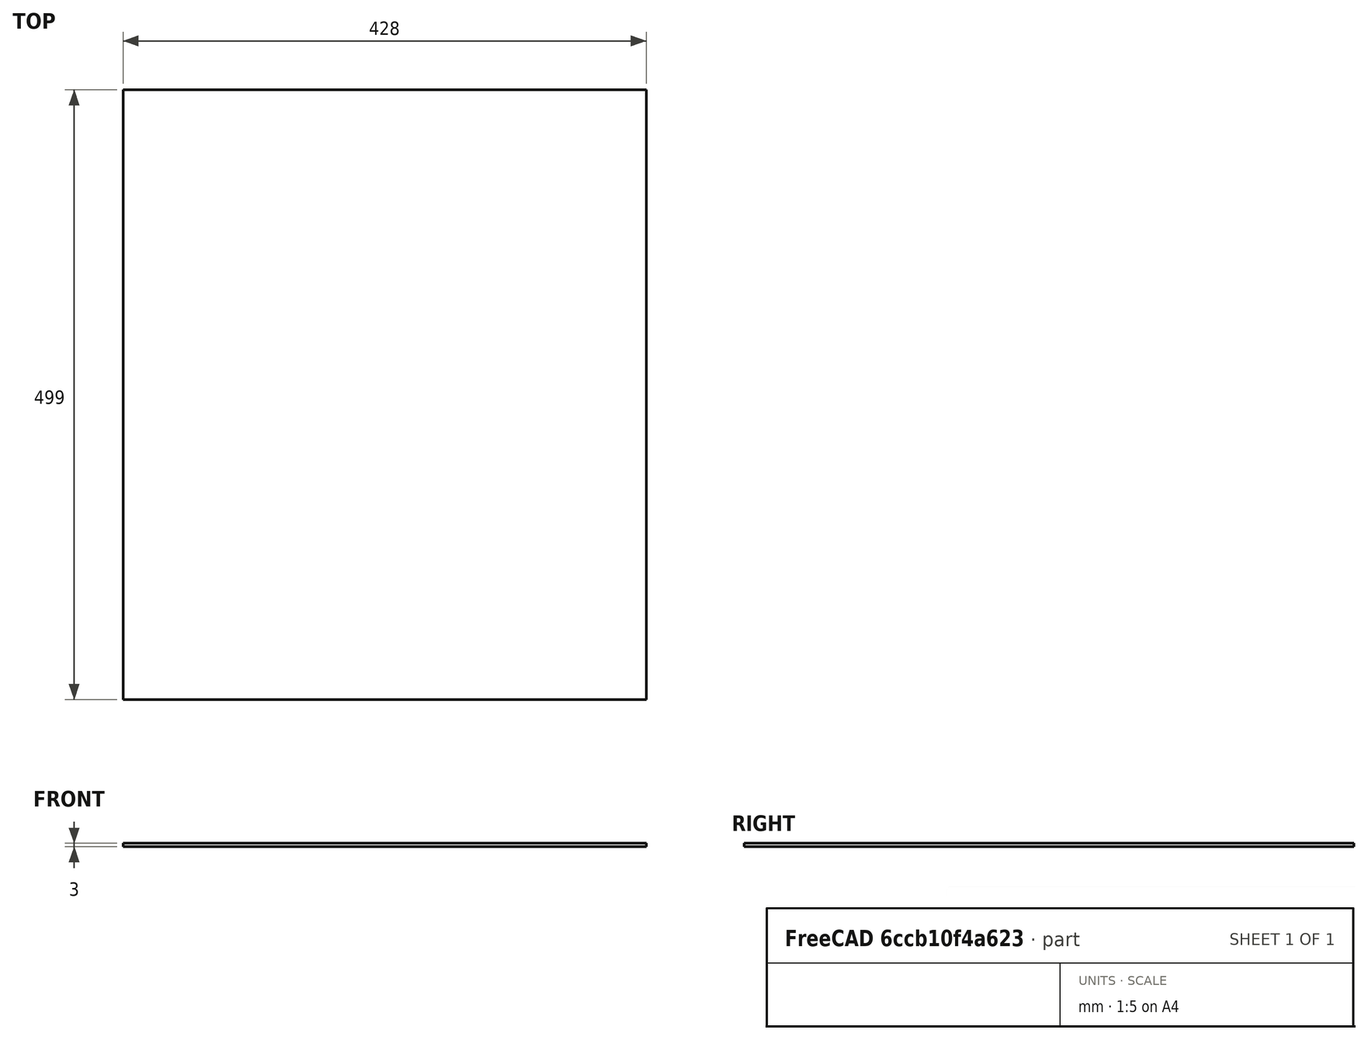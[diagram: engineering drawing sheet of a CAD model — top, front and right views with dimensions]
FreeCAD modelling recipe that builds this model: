
FCSTD DOCUMENT  (FreeCAD 0.19R)
Label: panj
License: All rights reserved
LicenseURL: http://en.wikipedia.org/wiki/All_rights_reserved
objects: App::Link×9, PartDesign::CoordinateSystem×4, App::DocumentObjectGroup×3, TechDraw::DrawSVGTemplate×3, TechDraw::DrawViewPart×3, TechDraw::DrawPage×3, App::Part×2, TechDraw::DrawViewSection×2, App::FeaturePython×1, Sketcher::SketchObject×1, PartDesign::Pad×1, PartDesign::Body×1
note: 8 computed .brp shape members not serialized (recipe doc carries the construction recipe); baked Part::Feature solids carry a one-line shape summary decoded from their .brp
EXTERNAL_REF file=podnica_ohisje.FCStd obj=LCS_bottom
EXTERNAL_REF file=podnica_ohisje.FCStd obj=Assembly
EXTERNAL_REF file=podnica_ohisje.FCStd obj=LCS_insert_low
EXTERNAL_REF file=smukalnik.FCStd obj=LCS_podnica
EXTERNAL_REF file=smukalnik.FCStd obj=Assembly
EXTERNAL_REF file=podnica_ohisje.FCStd obj=LCS_insert
EXTERNAL_REF file=smukalnik_mreza.FCStd obj=LCS_spreaj
EXTERNAL_REF file=smukalnik_mreza.FCStd obj=Assembly
EXTERNAL_REF file=podnica_ohisje.FCStd obj=LCS_pokrovcek
EXTERNAL_REF file=podnica_pokrovcek.FCStd obj=LCS_Origin
EXTERNAL_REF file=podnica_pokrovcek.FCStd obj=Assembly
EXTERNAL_REF file=naklada.FCStd obj=LCS_Origin
EXTERNAL_REF file=podnica_ohisje.FCStd obj=LCS_Origin
EXTERNAL_REF file=naklada.FCStd obj=Assembly
EXTERNAL_REF file=naklada.FCStd obj=LCS_1
EXTERNAL_REF file=naklada_nizka.FCStd obj=LCS_Origin
EXTERNAL_REF file=naklada_nizka.FCStd obj=Assembly
EXTERNAL_REF file=naklada_nizka.FCStd obj=LCS_1
EXTERNAL_REF file=pokrov.FCStd obj=LCS_botton
EXTERNAL_REF file=pokrov.FCStd obj=Assembly
EXTERNAL_REF file=pokrov.FCStd obj=LCS_1
EXTERNAL_REF file=streha.FCStd obj=LCS_Origin
EXTERNAL_REF file=streha.FCStd obj=Assembly

FEATURE [PartDesign::CoordinateSystem] LCS_Origin
  AttacherType = Attacher::AttachEngine3D
  MapMode = 2
  Support = -> [X_Axis]
FEATURE [App::FeaturePython] Variables  # WARN: FeaturePython — macro-defined, semantics opaque (R4)
  Type = App::PropertyContainer
FEATURE [App::DocumentObjectGroup] Constraints
FEATURE [App::DocumentObjectGroup] Configurations
FEATURE [App::Link] podnica_ohisje
  AttachedBy = #LCS_bottom
  AttachedTo = Parent Assembly#LCS_Origin
  LinkPlacement = pos=(0,0,120) rot=(0,0,1;0rad)
  LinkedObject = -> <external podnica_ohisje.FCStd>#Assembly
  Placement = pos=(0,0,120) rot=(0,0,1;0rad)
  SolverId = Asm4EE
  expr: Placement = LCS_Origin.Placement * AttachmentOffset * podnica_ohisje#LCS_bottom.Placement ^ -1
FEATURE [App::Link] smukalnik
  AttachedBy = #LCS_podnica
  AttachedTo = podnica_ohisje#LCS_insert_low
  LinkPlacement = pos=(0,-234,65) rot=(0,0,1;0rad)
  LinkedObject = -> <external smukalnik.FCStd>#Assembly
  Placement = pos=(0,-234,65) rot=(0,0,1;0rad)
  SolverId = Asm4EE
  expr: Placement = podnica_ohisje.Placement * podnica_ohisje#LCS_insert_low.Placement * AttachmentOffset * smukalnik#LCS_podnica.Placement ^ -1
FEATURE [App::Link] smukalnik_mreza
  AttachedBy = #LCS_spreaj
  AttachedTo = podnica_ohisje#LCS_insert
  LinkPlacement = pos=(0,18.5,35) rot=(0,0,1;0rad)
  LinkedObject = -> <external smukalnik_mreza.FCStd>#Assembly
  Placement = pos=(0,18.5,35) rot=(0,0,1;0rad)
  SolverId = Asm4EE
  expr: Placement = podnica_ohisje.Placement * podnica_ohisje#LCS_insert.Placement * AttachmentOffset * smukalnik_mreza#LCS_spreaj.Placement ^ -1
FEATURE [App::Link] podnica_pokrovcek
  AttachedBy = #LCS_Origin
  AttachedTo = podnica_ohisje#LCS_pokrovcek
  LinkPlacement = pos=(0,-252,35) rot=(0,0,1;0rad)
  LinkedObject = -> <external podnica_pokrovcek.FCStd>#Assembly
  Placement = pos=(0,-252,35) rot=(0,0,1;0rad)
  SolverId = Asm4EE
  expr: Placement = podnica_ohisje.Placement * podnica_ohisje#LCS_pokrovcek.Placement * AttachmentOffset * podnica_pokrovcek#LCS_Origin.Placement ^ -1
FEATURE [App::Link] naklada
  AttachedBy = #LCS_Origin
  AttachedTo = podnica_ohisje#LCS_Origin
  LinkPlacement = pos=(0,0,120) rot=(0,0,1;0rad)
  LinkedObject = -> <external naklada.FCStd>#Assembly
  Placement = pos=(0,0,120) rot=(0,0,1;0rad)
  SolverId = Asm4EE
  expr: Placement = podnica_ohisje.Placement * podnica_ohisje#LCS_Origin.Placement * AttachmentOffset * naklada#LCS_Origin.Placement ^ -1
FEATURE [PartDesign::CoordinateSystem] LCS_0  label="LCS_bottom"
  AttacherType = Attacher::AttachEngine3D
  MapMode = 2
  Support = -> [X_Axis001]
FEATURE [PartDesign::CoordinateSystem] LCS_0001
  AttacherType = Attacher::AttachEngine3D
  MapMode = 2
  Support = -> [X_Axis002]
FEATURE [Sketcher::SketchObject] Sketch
  FullyConstrained = true
  MapMode = 5
  Support = -> [XY_Plane002]
  sketch-geometry (4):
    g0: LineSegment StartX=-214 StartY=-249.5 StartZ=0 EndX=214 EndY=-249.5 EndZ=0
    g1: LineSegment StartX=214 StartY=-249.5 StartZ=0 EndX=214 EndY=249.5 EndZ=0
    g2: LineSegment StartX=214 StartY=249.5 StartZ=0 EndX=-214 EndY=249.5 EndZ=0
    g3: LineSegment StartX=-214 StartY=249.5 StartZ=0 EndX=-214 EndY=-249.5 EndZ=0
  constraints (10):
    c: Coincident(g0,g1)
    c: Coincident(g1,g2)
    c: Coincident(g2,g3)
    c: Coincident(g3,g0)
    c: Horizontal(g2)
    c: Vertical(g3)
    c: Symmetric(g0,g0,g-2)
    c: Symmetric(g0,g1,g-1)
    c: DistanceX(g2,g2) = 428
    c: DistanceY(g1,g1) = 499
FEATURE [PartDesign::Pad] Pad
  Direction = (1,1,1)
  Length = 3
  Length2 = 100
  Profile = -> Sketch
  Type = 0
FEATURE [PartDesign::Body] Body
  Group = -> [LCS_0001,Sketch,Pad]
  Origin = -> Origin002
  Tip = -> Pad
FEATURE [PartDesign::CoordinateSystem] LCS_1  label="LCS_up"
  AttacherType = Attacher::AttachEngine3D
  Placement = pos=(0,0,3) rot=(0,0,1;0rad)
FEATURE [App::Part] maticna_resetka
  Group = -> [LCS_0,Body,LCS_1]
  Origin = -> Origin001
FEATURE [App::DocumentObjectGroup] Parts
  Group = -> [maticna_resetka]
FEATURE [App::Link] maticna_resetka001
  AssemblyType = Part::Link
  AttachedBy = #LCS_0
  AttachedTo = naklada#LCS_1
  LinkPlacement = pos=(0,0,420) rot=(0,0,1;0rad)
  LinkedObject = -> maticna_resetka
  Placement = pos=(0,0,420) rot=(0,0,1;0rad)
  SolverId = Asm4EE
  expr: Placement = naklada.Placement * naklada#LCS_1.Placement * AttachmentOffset * LCS_0.Placement ^ -1
FEATURE [App::Link] naklada_nizka
  AttachedBy = #LCS_Origin
  AttachedTo = maticna_resetka001#LCS_1
  LinkPlacement = pos=(0,0,423) rot=(0,0,1;0rad)
  LinkedObject = -> <external naklada_nizka.FCStd>#Assembly
  Placement = pos=(0,0,423) rot=(0,0,1;0rad)
  SolverId = Asm4EE
  expr: Placement = maticna_resetka001.Placement * LCS_1.Placement * AttachmentOffset * naklada_nizka#LCS_Origin.Placement ^ -1
FEATURE [App::Link] pokrov
  AttachedBy = #LCS_botton
  AttachedTo = naklada_nizka#LCS_1
  LinkPlacement = pos=(0,0,641) rot=(0,0,1;0rad)
  LinkedObject = -> <external pokrov.FCStd>#Assembly
  Placement = pos=(0,0,641) rot=(0,0,1;0rad)
  SolverId = Asm4EE
  expr: Placement = naklada_nizka.Placement * naklada_nizka#LCS_1.Placement * AttachmentOffset * pokrov#LCS_botton.Placement ^ -1
FEATURE [App::Link] streha
  AttachedBy = #LCS_Origin
  AttachedTo = pokrov#LCS_1
  LinkPlacement = pos=(0,0,701) rot=(0,0,1;0rad)
  LinkedObject = -> <external streha.FCStd>#Assembly
  Placement = pos=(0,0,701) rot=(0,0,1;0rad)
  SolverId = Asm4EE
  expr: Placement = pokrov.Placement * pokrov#LCS_1.Placement * AttachmentOffset * streha#LCS_Origin.Placement ^ -1
FEATURE [App::Part] Assembly
  AssemblyType = Part::Link
  Group = -> [LCS_Origin,Variables,Constraints,Configurations,podnica_ohisje,smukalnik,smukalnik_mreza,podnica_pokrovcek,naklada,maticna_resetka001,naklada_nizka,pokrov,streha]
  Origin = -> Origin
  Type = Assembly
FEATURE [TechDraw::DrawSVGTemplate] Template
  EditableTexts = AVTOR=Brane Borštnik; AVTOR_2=Risal: Janez Paternoster; DATUM=6.5.2022; MERILO=1:4; NAZIV=Dadant-Blatt panj; STRAN=Stran 1/3; VIR=https://github.com/<owner>/Dadant-Blatt
  Height = 297
  Orientation = 0
  Width = 210
FEATURE [TechDraw::DrawViewPart] View
  CoarseView = false
  Direction = (0.577,-0.577,0.577)
  Focus = 100
  HardHidden = false
  IsoCount = 0
  IsoHidden = false
  IsoVisible = false
  LockPosition = false
  Perspective = false
  Rotation = 0
  Scale = 0.25
  ScaleType = 0
  SeamHidden = false
  SeamVisible = true
  SmoothHidden = false
  SmoothVisible = true
  Source = -> [Assembly]
  X = 112.091
  XDirection = (0.707,0.707,0)
  Y = 158.928
FEATURE [TechDraw::DrawPage] Page  label="Page1"
  KeepUpdated = true
  NextBalloonIndex = 1
  ProjectionType = 0
  Scale = 0.25
  Template = -> Template
  Views = -> [View]
FEATURE [TechDraw::DrawSVGTemplate] Template001
  EditableTexts = AVTOR=Brane Borštnik; AVTOR_2=Risal: Janez Paternoster; DATUM=6.5.2022; MERILO=1:3,33; NAZIV=Dadant-Blatt panj; STRAN=Stran 2/3; VIR=https://github.com/<owner>/Dadant-Blatt
  Height = 297
  Orientation = 0
  Width = 210
FEATURE [TechDraw::DrawViewPart] View002
  CoarseView = false
  Direction = (0,-1,0)
  Focus = 100
  HardHidden = false
  IsoCount = 0
  IsoHidden = false
  IsoVisible = false
  LockPosition = false
  Perspective = false
  Rotation = 0
  Scale = 0.3
  ScaleType = 0
  SeamHidden = false
  SeamVisible = true
  SmoothHidden = false
  SmoothVisible = true
  Source = -> [Assembly]
  X = -84.3792
  XDirection = (1,0,0)
  Y = 158.511
FEATURE [TechDraw::DrawViewSection] SectionView  label="Section  - "
  BaseView = -> View002
  CoarseView = false
  CutSurfaceDisplay = 2
  Direction = (-1,0,0)
  FileGeomPattern = <path>
  FileHatchPattern = <path>
  Focus = 100
  FuseBeforeCut = false
  HardHidden = false
  HatchScale = 1
  IsoCount = 0
  IsoHidden = false
  IsoVisible = false
  LockPosition = false
  NameGeomPattern = Diamant
  Perspective = false
  Rotation = 0
  Scale = 0.3
  ScaleType = 0
  SeamHidden = false
  SeamVisible = true
  SectionDirection = 0
  SectionNormal = (-1,0,0)
  SectionOrigin = (0,-25,359.5)
  SmoothHidden = false
  SmoothVisible = true
  Source = -> [Assembly]
  X = 113.76
  XDirection = (0,-1,0)
  Y = 161.014
FEATURE [TechDraw::DrawPage] Page001  label="Page2"
  KeepUpdated = true
  NextBalloonIndex = 1
  ProjectionType = 0
  Scale = 0.3
  Template = -> Template001
  Views = -> [View002,SectionView]
FEATURE [TechDraw::DrawSVGTemplate] Template002
  EditableTexts = AVTOR=Brane Borštnik; AVTOR_2=Risal: Janez Paternoster; DATUM=6.5.2022; MERILO=1:3,33; NAZIV=Dadant-Blatt panj; STRAN=Stran 3/3; VIR=https://github.com/<owner>/Dadant-Blatt
  Height = 297
  Orientation = 0
  Width = 210
FEATURE [TechDraw::DrawViewPart] View003
  CoarseView = false
  Direction = (1,0,0)
  Focus = 100
  HardHidden = false
  IsoCount = 0
  IsoHidden = false
  IsoVisible = false
  LockPosition = false
  Perspective = false
  Rotation = 0
  Scale = 0.3
  ScaleType = 0
  SeamHidden = false
  SeamVisible = true
  SmoothHidden = false
  SmoothVisible = true
  Source = -> [Assembly]
  X = -108.156
  XDirection = (0,1,0)
  Y = 148.083
FEATURE [TechDraw::DrawViewSection] SectionView001  label="Section  - 001"
  BaseView = -> View003
  CoarseView = false
  CutSurfaceDisplay = 2
  Direction = (0,-1,0)
  FileGeomPattern = <path>
  FileHatchPattern = <path>
  Focus = 100
  FuseBeforeCut = false
  HardHidden = false
  HatchScale = 1
  IsoCount = 0
  IsoHidden = false
  IsoVisible = false
  LockPosition = false
  NameGeomPattern = Diamant
  Perspective = false
  Rotation = 0
  Scale = 0.3
  ScaleType = 0
  SeamHidden = false
  SeamVisible = true
  SectionDirection = 0
  SectionNormal = (0,-1,0)
  SectionOrigin = (0,-25,359.5)
  SmoothHidden = false
  SmoothVisible = true
  Source = -> [Assembly]
  X = 111.674
  XDirection = (1,0,0)
  Y = 160.18
FEATURE [TechDraw::DrawPage] Page002  label="Page3"
  KeepUpdated = true
  NextBalloonIndex = 1
  ProjectionType = 0
  Scale = 0.3
  Template = -> Template002
  Views = -> [View003,SectionView001]
note: 4 file-system paths scrubbed to <path> (originals preserved in the JSON sidecar)

RESOLVED EXTERNAL PARTS (link-assembly join: the EXTERNAL_REF files above that resolve inside this repo's crawl, each included once):
---- part naklada.FCStd = doc fcstd_21cce96157d1 (61008 chars; too large to inline — full recipe in that document) ----
---- part naklada_nizka.FCStd = doc fcstd_ec1ecf22dc17 (61010 chars; too large to inline — full recipe in that document) ----
---- part podnica_pokrovcek.FCStd = doc fcstd_f92a410cbc04 ----
FCSTD DOCUMENT  (FreeCAD 0.19R)
Label: podnica_pokrovcek
License: All rights reserved
LicenseURL: http://en.wikipedia.org/wiki/All_rights_reserved
objects: App::Link×13, PartDesign::Line×12, TechDraw::DrawViewDimension×9, Sketcher::SketchObject×6, PartDesign::CoordinateSystem×6, TechDraw::DrawProjGroupItem×6, TechDraw::DrawRichAnno×5, App::Part×4, PartDesign::Body×3, App::DocumentObjectGroup×3, TechDraw::DrawProjGroup×3, PartDesign::Pad×2, TechDraw::DrawSVGTemplate×1, PartDesign::Pocket×1, App::FeaturePython×1, PartDesign::Revolution×1, TechDraw::DrawPage×1
note: 35 computed .brp shape members not serialized (recipe doc carries the construction recipe); baked Part::Feature solids carry a one-line shape summary decoded from their .brp

FEATURE [PartDesign::Body] Body
  Origin = -> Origin001
FEATURE [Sketcher::SketchObject] Sketch
  FullyConstrained = true
  MapMode = 5
  Placement = pos=(0,0,0) rot=(1,0,0;1.5708rad)
  Support = -> [XZ_Plane001]
  sketch-geometry (8):
    g0: LineSegment StartX=-186.5 StartY=0 StartZ=0 EndX=-186.5 EndY=68 EndZ=0
    g1: LineSegment StartX=-186.5 StartY=68 StartZ=0 EndX=186.5 EndY=68 EndZ=0
    g2: LineSegment StartX=186.5 StartY=68 StartZ=0 EndX=186.5 EndY=0 EndZ=0
    g3: LineSegment StartX=186.5 StartY=0 StartZ=0 EndX=60 EndY=0 EndZ=0
    g4: LineSegment StartX=60 StartY=0 StartZ=0 EndX=60 EndY=7 EndZ=0
    g5: LineSegment StartX=60 StartY=7 StartZ=0 EndX=-60 EndY=7 EndZ=0
    g6: LineSegment StartX=-60 StartY=7 StartZ=0 EndX=-60 EndY=0 EndZ=0
    g7: LineSegment StartX=-60 StartY=0 StartZ=0 EndX=-186.5 EndY=0 EndZ=0
  constraints (23):
    c: Vertical(g0)
    c: Coincident(g0,g1)
    c: Horizontal(g1)
    c: Coincident(g1,g2)
    c: Vertical(g2)
    c: Coincident(g2,g3)
    c: Horizontal(g3)
    c: Coincident(g3,g4)
    c: Vertical(g4)
    c: Coincident(g4,g5)
    c: Horizontal(g5)
    c: Coincident(g5,g6)
    c: Vertical(g6)
    c: Coincident(g6,g7)
    c: Coincident(g7,g0)
    c: Horizontal(g7)
    c: Symmetric(g6,g3,g-1)
    c: Horizontal(g6,g3)
    c: Equal(g7,g3)
    c: DistanceY(g4,g4) = 7  'H2'
    c: DistanceX(g5,g5) = 120  'L2'
    c: DistanceY(g0,g0) = 68  'H'
    c: DistanceX(g1,g1) = 373  'L'
FEATURE [PartDesign::Pad] Pad
  Direction = (1,1,1)
  Length = 18
  Length2 = 100
  Placement = pos=(0,0,0) rot=(1,0,0;1.5708rad)
  Profile = -> Sketch
  Reversed = true
  Type = 0
FEATURE [TechDraw::DrawSVGTemplate] Template
  EditableTexts = AVTOR=Brane Borštnik,AVTOR_2=Risal: Janez Paternoster,DATUM=6.5.2022,MATERIAL=Les, smreka,MERILO=1:2,NAZIV=Pokrovček v podnici,+3 more (map truncated)
  Height = 210
  Orientation = 1
  Width = 297
FEATURE [Sketcher::SketchObject] Sketch001
  FullyConstrained = true
  MapMode = 5
  Placement = pos=(0,0,0) rot=(1,0,0;1.5708rad)
  Support = -> [XZ_Plane001]
  sketch-geometry (23):
    g0: Circle CenterX=-165 CenterY=56 CenterZ=0 NormalX=0 NormalY=0 NormalZ=1 AngleXU=0 Radius=5.5
    g1: Circle CenterX=-135 CenterY=56 CenterZ=0 NormalX=0 NormalY=0 NormalZ=1 AngleXU=0 Radius=5.5
    g2: Circle CenterX=-105 CenterY=56 CenterZ=0 NormalX=0 NormalY=0 NormalZ=1 AngleXU=0 Radius=5.5
    g3: Circle CenterX=-75 CenterY=56 CenterZ=0 NormalX=0 NormalY=0 NormalZ=1 AngleXU=0 Radius=5.5
    g4: Circle CenterX=-45 CenterY=56 CenterZ=0 NormalX=0 NormalY=0 NormalZ=1 AngleXU=0 Radius=5.5
    g5: Circle CenterX=-15 CenterY=56 CenterZ=0 NormalX=0 NormalY=0 NormalZ=1 AngleXU=0 Radius=5.5
    g6: Circle CenterX=15 CenterY=56 CenterZ=0 NormalX=0 NormalY=0 NormalZ=1 AngleXU=0 Radius=5.5
    g7: Circle CenterX=45 CenterY=56 CenterZ=0 NormalX=0 NormalY=0 NormalZ=1 AngleXU=0 Radius=5.5
    g8: Circle CenterX=75 CenterY=56 CenterZ=0 NormalX=0 NormalY=0 NormalZ=1 AngleXU=0 Radius=5.5
    g9: Circle CenterX=105 CenterY=56 CenterZ=0 NormalX=0 NormalY=0 NormalZ=1 AngleXU=0 Radius=5.5
    g10: Circle CenterX=135 CenterY=56 CenterZ=0 NormalX=0 NormalY=0 NormalZ=1 AngleXU=0 Radius=5.5
    g11: Circle CenterX=165 CenterY=56 CenterZ=0 NormalX=0 NormalY=0 NormalZ=1 AngleXU=0 Radius=5.5
    g12: LineSegment StartX=-165 StartY=56 StartZ=0 EndX=-135 EndY=56 EndZ=0
    g13: LineSegment StartX=-135 StartY=56 StartZ=0 EndX=-105 EndY=56 EndZ=0
    g14: LineSegment StartX=-105 StartY=56 StartZ=0 EndX=-75 EndY=56 EndZ=0
    g15: LineSegment StartX=-75 StartY=56 StartZ=0 EndX=-45 EndY=56 EndZ=0
    g16: LineSegment StartX=-45 StartY=56 StartZ=0 EndX=-15 EndY=56 EndZ=0
    g17: LineSegment StartX=-15 StartY=56 StartZ=0 EndX=15 EndY=56 EndZ=0
    g18: LineSegment StartX=15 StartY=56 StartZ=0 EndX=45 EndY=56 EndZ=0
    g19: LineSegment StartX=45 StartY=56 StartZ=0 EndX=75 EndY=56 EndZ=0
    g20: LineSegment StartX=75 StartY=56 StartZ=0 EndX=105 EndY=56 EndZ=0
    g21: LineSegment StartX=105 StartY=56 StartZ=0 EndX=135 EndY=56 EndZ=0
    g22: LineSegment StartX=135 StartY=56 StartZ=0 EndX=165 EndY=56 EndZ=0
  constraints (50):
    c: Horizontal(g12)
    c: Coincident(g12,g13)
    c: Horizontal(g13)
    c: Coincident(g13,g14)
    c: Horizontal(g14)
    c: Coincident(g14,g15)
    c: Coincident(g15,g16)
    c: Horizontal(g16)
    c: Coincident(g16,g17)
    c: Coincident(g17,g18)
    c: Horizontal(g18)
    c: Coincident(g18,g19)
    c: Horizontal(g19)
    c: Coincident(g19,g20)
    c: Horizontal(g20)
    c: Coincident(g20,g21)
    c: Horizontal(g21)
    c: Coincident(g21,g22)
    c: Horizontal(g22)
    c: Horizontal(g15)
    c: Symmetric(g16,g17,g-2)
    c: Equal(g17,g16)
    c: Equal(g17,g15)
    c: Equal(g17,g14)
    c: Equal(g17,g13)
    c: Equal(g17,g12)
    c: Equal(g17, g18-g22) x5
    c: Coincident(g0,g12)
    c: Coincident(g1,g12)
    c: Coincident(g2,g13)
    c: Coincident(g3,g14)
    c: Coincident(g4,g15)
    c: Coincident(g5,g16)
    c: Coincident(g6,g17)
    c: Coincident(g18,g7)
    c: Coincident(g8,g19)
    c: Coincident(g9,g20)
    c: Coincident(g22,g11)
    c: Coincident(g10,g21)
    c: Equal(g5,g4)
    c: Equal(g5,g3)
    c: Equal(g5,g2)
    c: Equal(g5,g1)
    c: Equal(g5,g0)
    c: Equal(g5,g6)
    c: Equal(g6, g7-g11) x5
    c: Diameter(g0) = 11
    c: DistanceX(g17,g17) = 30
    c: DistanceX(g0,g11) = 330
    c: DistanceY(g-1,g0) = 56
FEATURE [PartDesign::Pocket] Pocket
  BaseFeature = -> Pad
  Length = 5
  Length2 = 100
  Placement = pos=(0,0,0) rot=(1,0,0;1.5708rad)
  Profile = -> Sketch001
  Type = 1
FEATURE [PartDesign::CoordinateSystem] LCS_Origin
  AttacherType = Attacher::AttachEngine3D
  MapMode = 2
  Support = -> [X_Axis002]
FEATURE [App::FeaturePython] Variables  # WARN: FeaturePython — macro-defined, semantics opaque (R4)
  Type = App::PropertyContainer
FEATURE [App::DocumentObjectGroup] Constraints
FEATURE [App::DocumentObjectGroup] Configurations
FEATURE [PartDesign::CoordinateSystem] LCS_0
  AttacherType = Attacher::AttachEngine3D
  MapMode = 2
  Support = -> [X_Axis003]
FEATURE [PartDesign::CoordinateSystem] LCS_0001
  AttacherType = Attacher::AttachEngine3D
  MapMode = 2
  Support = -> [X_Axis004]
FEATURE [Sketcher::SketchObject] Sketch004
  FullyConstrained = true
  MapMode = 5
  Placement = pos=(0,0,0) rot=(1,0,0;1.5708rad)
  Support = -> [XZ_Plane004]
  expr: Constraints[18] = Sketch.Constraints.L
  expr: Constraints[19] = Sketch.Constraints.H
  expr: Constraints[20] = Sketch.Constraints.L2
  expr: Constraints[21] = Sketch.Constraints.H2
  sketch-geometry (8):
    g0: LineSegment StartX=-186.5 StartY=68 StartZ=0 EndX=186.5 EndY=68 EndZ=0
    g1: LineSegment StartX=186.5 StartY=68 StartZ=0 EndX=186.5 EndY=0 EndZ=0
    g2: LineSegment StartX=186.5 StartY=0 StartZ=0 EndX=60 EndY=0 EndZ=0
    g3: LineSegment StartX=60 StartY=0 StartZ=0 EndX=60 EndY=7 EndZ=0
    g4: LineSegment StartX=60 StartY=7 StartZ=0 EndX=-60 EndY=7 EndZ=0
    g5: LineSegment StartX=-60 StartY=7 StartZ=0 EndX=-60 EndY=0 EndZ=0
    g6: LineSegment StartX=-60 StartY=0 StartZ=0 EndX=-186.5 EndY=0 EndZ=0
    g7: LineSegment StartX=-186.5 StartY=0 StartZ=0 EndX=-186.5 EndY=68 EndZ=0
  constraints (23):
    c: Horizontal(g0)
    c: Coincident(g0,g1)
    c: Vertical(g1)
    c: Coincident(g1,g2)
    c: Horizontal(g2)
    c: Coincident(g2,g3)
    c: Vertical(g3)
    c: Coincident(g3,g4)
    c: Horizontal(g4)
    c: Coincident(g4,g5)
    c: Vertical(g5)
    c: Coincident(g5,g6)
    c: Horizontal(g6)
    c: Coincident(g6,g7)
    c: Coincident(g7,g0)
    c: Vertical(g7)
    c: Horizontal(g5,g2)
    c: Symmetric(g2,g5,g-1)
    c: DistanceX(g0,g0) = 373
    c: DistanceY(g7,g7) = 68
    c: DistanceX(g4,g4) = 120
    c: DistanceY(g5,g5) = 7
    c: Equal(g6,g2)
FEATURE [PartDesign::Pad] Pad001
  Direction = (1,1,1)
  Length = 18
  Length2 = 100
  Placement = pos=(0,0,0) rot=(1,0,0;1.5708rad)
  Profile = -> Sketch004
  Reversed = true
  Type = 0
  expr: Length = Pad.Length
FEATURE [Sketcher::SketchObject] Sketch005
  FullyConstrained = true
  MapMode = 5
  Placement = pos=(0,0,0) rot=(0.57735,0.57735,0.57735;2.0944rad)
  Support = -> [YZ_Plane004]
  sketch-geometry (4):
    g0: LineSegment StartX=-32.6227 StartY=0 StartZ=0 EndX=17 EndY=6.1307 EndZ=0
    g1: LineSegment StartX=17 StartY=6.1307 StartZ=0 EndX=16.7548 EndY=8.11561 EndZ=0
    g2: LineSegment StartX=16.7548 StartY=8.11561 StartZ=0 EndX=-32.868 EndY=1.98491 EndZ=0
    g3: LineSegment StartX=-32.868 StartY=1.98491 StartZ=0 EndX=-32.6227 EndY=0 EndZ=0
  constraints (12):
    c: Coincident(g0,g1)
    c: Coincident(g1,g2)
    c: Coincident(g2,g3)
    c: Coincident(g3,g0)
    c: Perpendicular(g1,g0)
    c: Perpendicular(g2,g1)
    c: Perpendicular(g3,g2)
    c: Distance(g-1,g0) = 4
    c: Distance(g-1,g2) = 6
    c: DistanceX(g-1,g0) = 17
    c: Distance(g2) = 50
    c: Horizontal(g0,g-1)
FEATURE [PartDesign::Body] Body_2
  Group = -> [LCS_0001,Sketch004,Pad001,Sketch005]
  Origin = -> Origin004
  Tip = -> Pad001
FEATURE [App::Part] pokrovcek_navaden
  Group = -> [LCS_0,Body_2]
  Origin = -> Origin003
FEATURE [PartDesign::CoordinateSystem] LCS_0002
  AttacherType = Attacher::AttachEngine3D
  MapMode = 2
  Support = -> [X_Axis005]
FEATURE [PartDesign::CoordinateSystem] LCS_0003
  AttacherType = Attacher::AttachEngine3D
  MapMode = 2
  Support = -> [X_Axis006]
FEATURE [Sketcher::SketchObject] Sketch006
  FullyConstrained = true
  MapMode = 5
  Placement = pos=(0,0,0) rot=(0.57735,0.57735,0.57735;2.0944rad)
  Support = -> [YZ_Plane006]
  sketch-geometry (5):
    g0: LineSegment StartX=-32.6227 StartY=0 StartZ=0 EndX=17 EndY=6.1307 EndZ=0
    g1: LineSegment StartX=17 StartY=6.1307 StartZ=0 EndX=16.7548 EndY=8.11561 EndZ=0
    g2: LineSegment StartX=16.7548 StartY=8.11561 StartZ=0 EndX=-32.868 EndY=1.98491 EndZ=0
    g3: LineSegment StartX=-32.868 StartY=1.98491 StartZ=0 EndX=-32.6227 EndY=0 EndZ=0
    g4: LineSegment StartX=-32.6227 StartY=-4.03041 StartZ=0 EndX=17 EndY=2.10028 EndZ=0
  constraints (16):
    c: Coincident(g0,g1)
    c: Coincident(g1,g2)
    c: Coincident(g2,g3)
    c: Coincident(g3,g0)
    c: Perpendicular(g1,g0)
    c: Perpendicular(g2,g1)
    c: Perpendicular(g3,g2)
    c: Distance(g-1,g0) = 4
    c: Distance(g-1,g2) = 6
    c: DistanceX(g-1,g0) = 17
    c: Distance(g2) = 50
    c: Horizontal(g0,g-1)
    c: PointOnObject(g-1,g4)
    c: Parallel(g4,g0)
    c: Vertical(g0,g4)
    c: Vertical(g0,g4)
FEATURE [PartDesign::Revolution] Revolution
  Angle = 360
  Axis = (1.52e-14,49.6227,6.1307)
  Base = (-1e-14,-32.6227,-4.03041)
  Placement = pos=(0,0,0) rot=(0.57735,0.57735,0.57735;2.0944rad)
  Profile = -> Sketch006
  ReferenceAxis = -> Sketch006 [Axis0]
FEATURE [App::Link] pokrovcek_smukalnik  label="pokrovcek_smukalnik001"
  AssemblyType = Part::Link
  LinkedObject = -> Part
FEATURE [PartDesign::CoordinateSystem] LCS_1
  AttacherType = Attacher::AttachEngine3D
FEATURE [PartDesign::Line] HoleAxis_1
  AttacherType = Attacher::AttachEngineLine
  Length = 15.4997
  MapMode = 19
  Placement = pos=(-165,1.24e-14,56) rot=(1,0,0;1.5708rad)
  ResizeMode = 1
  Support = -> [Pocket]
FEATURE [App::Link] cevka002  label="cevka1"
  AssemblyType = Part::Link
  AttachedBy = #LCS_0002
  AttachedTo = pokrovcek_smukalnik#HoleAxis_1
  AttachmentOffset = pos=(0,0,0) rot=(1,0,0;4.71239rad)
  LinkPlacement = pos=(-165,3.73e-14,56) rot=(0,0,1;0rad)
  LinkedObject = -> cevka
  Placement = pos=(-165,3.73e-14,56) rot=(0,0,1;0rad)
  SolverId = Asm4EE
  expr: Placement = pokrovcek_smukalnik.Placement * HoleAxis_1.Placement * AttachmentOffset * LCS_0002.Placement ^ -1
FEATURE [PartDesign::Line] HoleAxis_2 .. HoleAxis_12  x11 (patterned run collapsed; names and placements below)
  AttacherType = Attacher::AttachEngineLine
  Length = 15.4997
  MapMode = 19
  ResizeMode = 1
  Support = -> [Pocket]
  placements: 11 in arithmetic series — first pos=(-135,1.24e-14,56) rot=(1,0,0;1.5708rad), step (30,0,0), last pos=(165,1.24e-14,56) rot=(1,0,0;1.5708rad)
FEATURE [App::Part] Part  label="pokrovcek_smukalnik"
  Group = -> [Body,LCS_1,Sketch001,Pocket,Pad,Sketch,HoleAxis_1,HoleAxis_2,HoleAxis_3,HoleAxis_4,HoleAxis_5,HoleAxis_6,HoleAxis_7,HoleAxis_8,HoleAxis_9,HoleAxis_10,HoleAxis_11,HoleAxis_12]
  Origin = -> Origin
FEATURE [TechDraw::DrawProjGroupItem] ProjItem  label="Front"
  CoarseView = false
  Direction = (0,-1,0)
  Focus = 100
  HardHidden = false
  IsoCount = 0
  IsoHidden = false
  IsoVisible = false
  LockPosition = true
  Perspective = false
  Rotation = 0
  RotationVector = (1,0,0)
  Scale = 0.5
  ScaleType = 2
  SeamHidden = false
  SeamVisible = true
  SmoothHidden = false
  SmoothVisible = true
  Source = -> [Part]
  Type = 0
  X = 0
  XDirection = (1,0,0)
  Y = 0
FEATURE [TechDraw::DrawProjGroupItem] ProjItem001  label="Left"
  CoarseView = false
  Direction = (-1,-1e-16,0)
  Focus = 100
  HardHidden = false
  IsoCount = 0
  IsoHidden = false
  IsoVisible = false
  LockPosition = false
  Perspective = false
  Rotation = 0
  RotationVector = (1,0,0)
  Scale = 0.5
  ScaleType = 2
  SeamHidden = false
  SeamVisible = true
  SmoothHidden = false
  SmoothVisible = true
  Source = -> [Part]
  Type = 1
  X = 127.75
  XDirection = (1e-16,-1,0)
  Y = 0
FEATURE [TechDraw::DrawProjGroup] ProjGroup
  Anchor = -> ProjItem
  AutoDistribute = true
  LockPosition = false
  ProjectionType = 0
  Rotation = 0
  Scale = 0.5
  ScaleType = 0
  Source = -> [Part]
  Views = -> [ProjItem,ProjItem001]
  X = 113.771
  Y = 141.789
  spacingX = 30
  spacingY = 15
FEATURE [TechDraw::DrawViewDimension] Dimension
  Arbitrary = false
  ArbitraryTolerances = false
  EqualTolerance = true
  FormatSpec = %.6g
  FormatSpecOverTolerance = %+.6g
  FormatSpecUnderTolerance = %+.6g
  Inverted = false
  LockPosition = false
  MeasureType = 1
  OverTolerance = 0
  References2D = -> [ProjItem001]
  Rotation = 0
  Scale = 0.5
  ScaleType = 0
  TheoreticalExact = false
  Type = 1
  UnderTolerance = 0
  X = -0.601719
  Y = 39.2636
FEATURE [TechDraw::DrawViewDimension] Dimension001
  Arbitrary = false
  ArbitraryTolerances = false
  EqualTolerance = true
  FormatSpec = %.6g
  FormatSpecOverTolerance = %+.6g
  FormatSpecUnderTolerance = %+.6g
  Inverted = false
  LockPosition = false
  MeasureType = 1
  OverTolerance = 0
  References2D = -> [ProjItem001]
  Rotation = 0
  Scale = 0.5
  ScaleType = 0
  TheoreticalExact = false
  Type = 2
  UnderTolerance = 0
  X = 16.2335
  Y = 1.80516
FEATURE [TechDraw::DrawViewDimension] Dimension002
  Arbitrary = false
  ArbitraryTolerances = false
  EqualTolerance = true
  FormatSpec = %.6g
  FormatSpecOverTolerance = %+.6g
  FormatSpecUnderTolerance = %+.6g
  Inverted = false
  LockPosition = false
  MeasureType = 1
  OverTolerance = 0
  References2D = -> [ProjItem]
  Rotation = 0
  Scale = 0.5
  ScaleType = 0
  TheoreticalExact = false
  Type = 1
  UnderTolerance = 0
  X = 0.902579
  Y = 42.5731
FEATURE [TechDraw::DrawViewDimension] Dimension003
  Arbitrary = false
  ArbitraryTolerances = false
  EqualTolerance = true
  FormatSpec = %.6g
  FormatSpecOverTolerance = %+.6g
  FormatSpecUnderTolerance = %+.6g
  Inverted = false
  LockPosition = false
  MeasureType = 1
  OverTolerance = 0
  References2D = -> [ProjItem]
  Rotation = 0
  Scale = 0.5
  ScaleType = 0
  TheoreticalExact = false
  Type = 1
  UnderTolerance = 0
  X = -2.10602
  Y = -25.8352
FEATURE [TechDraw::DrawViewDimension] Dimension004
  Arbitrary = false
  ArbitraryTolerances = false
  EqualTolerance = true
  FormatSpec = %.6g
  FormatSpecOverTolerance = %+.6g
  FormatSpecUnderTolerance = %+.6g
  Inverted = false
  LockPosition = false
  MeasureType = 1
  OverTolerance = 0
  References2D = -> [ProjItem]
  Rotation = 0
  Scale = 0.5
  ScaleType = 0
  TheoreticalExact = false
  Type = 2
  UnderTolerance = 0
  X = -36.6189
  Y = -27.5852
FEATURE [TechDraw::DrawViewDimension] Dimension005
  Arbitrary = false
  ArbitraryTolerances = false
  EqualTolerance = true
  FormatSpec = %.6g
  FormatSpecOverTolerance = %+.6g
  FormatSpecUnderTolerance = %+.6g
  Inverted = false
  LockPosition = false
  MeasureType = 1
  OverTolerance = 0
  References2D = -> [ProjItem]
  Rotation = 0
  Scale = 0.5
  ScaleType = 0
  TheoreticalExact = false
  Type = 1
  UnderTolerance = 0
  X = -0.30086
  Y = 34.1662
FEATURE [TechDraw::DrawViewDimension] Dimension006
  Arbitrary = false
  ArbitraryTolerances = false
  EqualTolerance = true
  FormatSpec = ⌀%.6g, 12x
  FormatSpecOverTolerance = %+.6g
  FormatSpecUnderTolerance = %+.6g
  Inverted = false
  LockPosition = false
  MeasureType = 1
  OverTolerance = 0
  References2D = -> [ProjItem]
  Rotation = 0
  Scale = 0.5
  ScaleType = 0
  TheoreticalExact = false
  Type = 5
  UnderTolerance = 0
  X = -75.5158
  Y = 28.5817
FEATURE [App::Link] cevka003
  AssemblyType = Part::Link
  AttachedBy = #LCS_0002
  AttachedTo = pokrovcek_smukalnik#HoleAxis_2
  AttachmentOffset = pos=(0,0,0) rot=(1,0,0;4.71239rad)
  LinkPlacement = pos=(-135,3.73e-14,56) rot=(0,0,1;0rad)
  LinkedObject = -> cevka
  Placement = pos=(-135,3.73e-14,56) rot=(0,0,1;0rad)
  SolverId = Asm4EE
  expr: Placement = pokrovcek_smukalnik.Placement * HoleAxis_2.Placement * AttachmentOffset * LCS_0002.Placement ^ -1
FEATURE [App::Link] cevka_2
  AssemblyType = Part::Link
  AttachedBy = #LCS_0002
  AttachedTo = pokrovcek_smukalnik#HoleAxis_3
  AttachmentOffset = pos=(0,0,0) rot=(1,0,0;4.71239rad)
  LinkPlacement = pos=(-105,3.73e-14,56) rot=(0,0,1;0rad)
  LinkedObject = -> cevka
  Placement = pos=(-105,3.73e-14,56) rot=(0,0,1;0rad)
  SolverId = Asm4EE
  expr: Placement = pokrovcek_smukalnik.Placement * HoleAxis_3.Placement * AttachmentOffset * LCS_0002.Placement ^ -1
FEATURE [App::Link] cevka_3
  AssemblyType = Part::Link
  AttachedBy = #LCS_0002
  AttachedTo = pokrovcek_smukalnik#HoleAxis_4
  AttachmentOffset = pos=(0,0,0) rot=(1,0,0;4.71239rad)
  LinkPlacement = pos=(-75,3.73e-14,56) rot=(0,0,1;0rad)
  LinkedObject = -> cevka
  Placement = pos=(-75,3.73e-14,56) rot=(0,0,1;0rad)
  SolverId = Asm4EE
  expr: Placement = pokrovcek_smukalnik.Placement * HoleAxis_4.Placement * AttachmentOffset * LCS_0002.Placement ^ -1
FEATURE [App::Link] cevka_4
  AssemblyType = Part::Link
  AttachedBy = #LCS_0002
  AttachedTo = pokrovcek_smukalnik#HoleAxis_5
  AttachmentOffset = pos=(0,0,0) rot=(1,0,0;4.71239rad)
  LinkPlacement = pos=(-45,3.73e-14,56) rot=(0,0,1;0rad)
  LinkedObject = -> cevka
  Placement = pos=(-45,3.73e-14,56) rot=(0,0,1;0rad)
  SolverId = Asm4EE
  expr: Placement = pokrovcek_smukalnik.Placement * HoleAxis_5.Placement * AttachmentOffset * LCS_0002.Placement ^ -1
FEATURE [App::Link] cevka_5
  AssemblyType = Part::Link
  AttachedBy = #LCS_0002
  AttachedTo = pokrovcek_smukalnik#HoleAxis_6
  AttachmentOffset = pos=(0,0,0) rot=(1,0,0;4.71239rad)
  LinkPlacement = pos=(-15,3.73e-14,56) rot=(0,0,1;0rad)
  LinkedObject = -> cevka
  Placement = pos=(-15,3.73e-14,56) rot=(0,0,1;0rad)
  SolverId = Asm4EE
  expr: Placement = pokrovcek_smukalnik.Placement * HoleAxis_6.Placement * AttachmentOffset * LCS_0002.Placement ^ -1
FEATURE [App::Link] cevka_6
  AssemblyType = Part::Link
  AttachedBy = #LCS_0002
  AttachedTo = pokrovcek_smukalnik#HoleAxis_7
  AttachmentOffset = pos=(0,0,0) rot=(1,0,0;4.71239rad)
  LinkPlacement = pos=(15,3.73e-14,56) rot=(0,0,1;0rad)
  LinkedObject = -> cevka
  Placement = pos=(15,3.73e-14,56) rot=(0,0,1;0rad)
  SolverId = Asm4EE
  expr: Placement = pokrovcek_smukalnik.Placement * HoleAxis_7.Placement * AttachmentOffset * LCS_0002.Placement ^ -1
FEATURE [App::Link] cevka_7
  AssemblyType = Part::Link
  AttachedBy = #LCS_0002
  AttachedTo = pokrovcek_smukalnik#HoleAxis_8
  AttachmentOffset = pos=(0,0,0) rot=(1,0,0;4.71239rad)
  LinkPlacement = pos=(45,3.73e-14,56) rot=(0,0,1;0rad)
  LinkedObject = -> cevka
  Placement = pos=(45,3.73e-14,56) rot=(0,0,1;0rad)
  SolverId = Asm4EE
  expr: Placement = pokrovcek_smukalnik.Placement * HoleAxis_8.Placement * AttachmentOffset * LCS_0002.Placement ^ -1
FEATURE [App::Link] cevka_8
  AssemblyType = Part::Link
  AttachedBy = #LCS_0002
  AttachedTo = pokrovcek_smukalnik#HoleAxis_9
  AttachmentOffset = pos=(0,0,0) rot=(1,0,0;4.71239rad)
  LinkPlacement = pos=(75,3.73e-14,56) rot=(0,0,1;0rad)
  LinkedObject = -> cevka
  Placement = pos=(75,3.73e-14,56) rot=(0,0,1;0rad)
  SolverId = Asm4EE
  expr: Placement = pokrovcek_smukalnik.Placement * HoleAxis_9.Placement * AttachmentOffset * LCS_0002.Placement ^ -1
FEATURE [App::Link] cevka_9
  AssemblyType = Part::Link
  AttachedBy = #LCS_0002
  AttachedTo = pokrovcek_smukalnik#HoleAxis_10
  AttachmentOffset = pos=(0,0,0) rot=(1,0,0;4.71239rad)
  LinkPlacement = pos=(105,3.73e-14,56) rot=(0,0,1;0rad)
  LinkedObject = -> cevka
  Placement = pos=(105,3.73e-14,56) rot=(0,0,1;0rad)
  SolverId = Asm4EE
  expr: Placement = pokrovcek_smukalnik.Placement * HoleAxis_10.Placement * AttachmentOffset * LCS_0002.Placement ^ -1
FEATURE [App::Link] cevka_10
  AssemblyType = Part::Link
  AttachedBy = #LCS_0002
  AttachedTo = pokrovcek_smukalnik#HoleAxis_11
  AttachmentOffset = pos=(0,0,0) rot=(1,0,0;4.71239rad)
  LinkPlacement = pos=(135,3.73e-14,56) rot=(0,0,1;0rad)
  LinkedObject = -> cevka
  Placement = pos=(135,3.73e-14,56) rot=(0,0,1;0rad)
  SolverId = Asm4EE
  expr: Placement = pokrovcek_smukalnik.Placement * HoleAxis_11.Placement * AttachmentOffset * LCS_0002.Placement ^ -1
FEATURE [App::Link] cevka_11
  AssemblyType = Part::Link
  AttachedBy = #LCS_0002
  AttachedTo = pokrovcek_smukalnik#HoleAxis_12
  AttachmentOffset = pos=(0,0,0) rot=(1,0,0;4.71239rad)
  LinkPlacement = pos=(165,3.73e-14,56) rot=(0,0,1;0rad)
  LinkedObject = -> cevka
  Placement = pos=(165,3.73e-14,56) rot=(0,0,1;0rad)
  SolverId = Asm4EE
  expr: Placement = pokrovcek_smukalnik.Placement * HoleAxis_12.Placement * AttachmentOffset * LCS_0002.Placement ^ -1
FEATURE [App::Part] Assembly
  AssemblyType = Part::Link
  Group = -> [LCS_Origin,Variables,Constraints,Configurations,pokrovcek_smukalnik,cevka002,cevka003,cevka_2,cevka_3,cevka_4,cevka_5,cevka_6,cevka_7,cevka_8,cevka_9,cevka_10,cevka_11]
  Origin = -> Origin002
  Type = Assembly
FEATURE [TechDraw::DrawProjGroupItem] ProjItem002  label="Front001"
  CoarseView = false
  Direction = (0,-1,0)
  Focus = 100
  HardHidden = false
  IsoCount = 0
  IsoHidden = false
  IsoVisible = false
  LockPosition = true
  Perspective = false
  Rotation = 0
  RotationVector = (1,0,0)
  ScaleType = 2
  SeamHidden = false
  SeamVisible = true
  SmoothHidden = false
  SmoothVisible = true
  Source = -> [pokrovcek_navaden]
  Type = 0
  X = 0
  XDirection = (1,0,0)
  Y = 0
FEATURE [TechDraw::DrawProjGroupItem] ProjItem003  label="Left001"
  CoarseView = false
  Direction = (-1,-1e-16,0)
  Focus = 100
  HardHidden = false
  IsoCount = 0
  IsoHidden = false
  IsoVisible = false
  LockPosition = false
  Perspective = false
  Rotation = 0
  RotationVector = (1,0,0)
  ScaleType = 2
  SeamHidden = false
  SeamVisible = true
  SmoothHidden = false
  SmoothVisible = true
  Source = -> [pokrovcek_navaden]
  Type = 1
  X = 112.75
  XDirection = (1e-16,-1,0)
  Y = 0
FEATURE [TechDraw::DrawProjGroup] ProjGroup001
  Anchor = -> ProjItem002
  AutoDistribute = true
  LockPosition = false
  ProjectionType = 0
  Rotation = 0
  Scale = 0.5
  ScaleType = 0
  Source = -> [pokrovcek_navaden]
  Views = -> [ProjItem002,ProjItem003]
  X = 114.804
  Y = 54.1547
  spacingX = 15
  spacingY = 15
FEATURE [Sketcher::SketchObject] Sketch007
  FullyConstrained = true
  MapMode = 5
  Placement = pos=(-9.1e-15,-32.1323,-3.96982) rot=(0.599592,0.599592,-0.530074;2.16676rad)
  Support = -> [Revolution]
FEATURE [PartDesign::Body] Body_3
  Group = -> [LCS_0003,Sketch006,Revolution,Sketch007]
  Origin = -> Origin006
  Tip = -> Revolution
FEATURE [App::Part] cevka
  Group = -> [LCS_0002,Body_3]
  Origin = -> Origin005
FEATURE [App::DocumentObjectGroup] Parts
  Group = -> [Part,pokrovcek_navaden,cevka]
FEATURE [TechDraw::DrawProjGroupItem] ProjItem007  label="Front004"
  CoarseView = false
  Direction = (0.997,-0.013,0.071)
  Focus = 100
  HardHidden = false
  IsoCount = 0
  IsoHidden = false
  IsoVisible = false
  LockPosition = true
  Perspective = false
  Rotation = 0
  RotationVector = (0.004,0.992,0.126)
  ScaleType = 2
  SeamHidden = false
  SeamVisible = true
  SmoothHidden = false
  SmoothVisible = true
  Source = -> [cevka]
  Type = 0
  X = 0
  XDirection = (0.004,0.992,0.126)
  Y = 0
FEATURE [TechDraw::DrawProjGroupItem] ProjItem008  label="Left002"
  CoarseView = false
  Direction = (-0.00396217,-0.992022,-0.126)
  Focus = 100
  HardHidden = false
  IsoCount = 0
  IsoHidden = false
  IsoVisible = false
  LockPosition = false
  Perspective = false
  Rotation = 0
  RotationVector = (1,0,0)
  ScaleType = 2
  SeamHidden = false
  SeamVisible = true
  SmoothHidden = false
  SmoothVisible = true
  Source = -> [cevka]
  Type = 1
  X = 30.568
  XDirection = (0.99739,-0.0130051,0.0710277)
  Y = 0
FEATURE [TechDraw::DrawProjGroup] ProjGroup004
  Anchor = -> ProjItem007
  AutoDistribute = true
  LockPosition = false
  ProjectionType = 0
  Rotation = 0
  Scale = 0.5
  ScaleType = 0
  Source = -> [cevka]
  Views = -> [ProjItem007,ProjItem008]
  X = 212.552
  Y = 95.1458
  spacingX = 15
  spacingY = 15
FEATURE [TechDraw::DrawViewDimension] Dimension009
  Arbitrary = false
  ArbitraryTolerances = false
  EqualTolerance = true
  FormatSpec = %.0f
  FormatSpecOverTolerance = %+.6g
  FormatSpecUnderTolerance = %+.6g
  Inverted = false
  LockPosition = false
  MeasureType = 1
  OverTolerance = 0
  References2D = -> [ProjItem007]
  Rotation = 0
  Scale = 0.5
  ScaleType = 0
  TheoreticalExact = false
  Type = 1
  UnderTolerance = 0
  X = 0.645995
  Y = 15.0715
FEATURE [TechDraw::DrawViewDimension] Dimension010
  Arbitrary = false
  ArbitraryTolerances = false
  EqualTolerance = true
  FormatSpec = ⌀%.0f
  FormatSpecOverTolerance = %+.6g
  FormatSpecUnderTolerance = %+.6g
  Inverted = false
  LockPosition = false
  MeasureType = 1
  OverTolerance = 0
  References2D = -> [ProjItem008]
  Rotation = 0
  Scale = 0.5
  ScaleType = 0
  TheoreticalExact = false
  Type = 5
  UnderTolerance = 0
  X = 13.033
  Y = 14.9402
FEATURE [TechDraw::DrawRichAnno] RichTextAnnotation
  AnnoParent = -> ProjItem007
  AnnoText = <!DOCTYPE HTML PUBLIC "-//W3C//DTD HTML 4.0//EN" "http://www.w3.org/TR/REC-html40/strict.dtd">\n<html><head><meta name="qrichtext" content="1" /><style type="text/css">\np, li { white-space: pre-wrap; }\n</style></head><body style=" font-family:'Ubuntu'; font-size:11pt; font-weight:400; font-style:normal;">\n<p style=" margin-top:0px; margin-bottom:0px; margin-left:0px; margin-right:0px; -qt-block-indent:0; text-indent:0px;"><span style=" font-size:10pt;">Cevke, 12 kom</span></p></body></html>
  LockPosition = false
  MaxWidth = -1
  Rotation = 0
  Scale = 0.5
  ScaleType = 0
  ShowFrame = false
  X = 19.8673
  Y = -10.8078
FEATURE [TechDraw::DrawRichAnno] RichTextAnnotation001
  AnnoParent = -> ProjItem
  AnnoText = <!DOCTYPE HTML PUBLIC "-//W3C//DTD HTML 4.0//EN" "http://www.w3.org/TR/REC-html40/strict.dtd">\n<html><head><meta name="qrichtext" content="1" /><style type="text/css">\np, li { white-space: pre-wrap; }\n</style></head><body style=" font-family:'Ubuntu'; font-size:11pt; font-weight:400; font-style:normal;">\n<p style=" margin-top:0px; margin-bottom:0px; margin-left:0px; margin-right:0px; -qt-block-indent:0; text-indent:0px;"><span style=" font-size:10pt;">Pokrovček za smukalnik.</span></p>\n<p style=" margin-top:0px; margin-bottom:0px; margin-left:0px; margin-right:0px; -qt-block-indent:0; text-indent:0px;"><span style=" font-size:10pt;">V luknje se vstavijo cevke,</span></p>\n<p style=" margin-top:0px; margin-bottom:0px; margin-left:0px; margin-right:0px; -qt-block-indent:0; text-indent:0px;"><span style=" font-size:10pt;">ki naj bodo obrnjene rahlo navzdol</span></p></body></html>
  LockPosition = false
  MaxWidth = -1
  Rotation = 0
  Scale = 0.5
  ScaleType = 0
  ShowFrame = false
  X = 49.9067
  Y = -3.81453
FEATURE [TechDraw::DrawRichAnno] RichTextAnnotation002
  AnnoParent = -> ProjItem002
  AnnoText = <!DOCTYPE HTML PUBLIC "-//W3C//DTD HTML 4.0//EN" "http://www.w3.org/TR/REC-html40/strict.dtd">\n<html><head><meta name="qrichtext" content="1" /><style type="text/css">\np, li { white-space: pre-wrap; }\n</style></head><body style=" font-family:'Ubuntu'; font-size:11pt; font-weight:400; font-style:normal;">\n<p style=" margin-top:0px; margin-bottom:0px; margin-left:0px; margin-right:0px; -qt-block-indent:0; text-indent:0px;"><span style=" font-size:10pt;">Navaden pokrovček na podnici</span></p></body></html>
  LockPosition = false
  MaxWidth = -1
  Rotation = 0
  Scale = 0.5
  ScaleType = 0
  ShowFrame = false
  X = 0
  Y = 0
FEATURE [TechDraw::DrawRichAnno] RichTextAnnotation003
  AnnoParent = -> ProjItem
  AnnoText = <!DOCTYPE HTML PUBLIC "-//W3C//DTD HTML 4.0//EN" "http://www.w3.org/TR/REC-html40/strict.dtd">\n<html><head><meta name="qrichtext" content="1" /><style type="text/css">\np, li { white-space: pre-wrap; }\n</style></head><body style=" font-family:'Ubuntu'; font-size:11pt; font-weight:400; font-style:normal;">\n<p style=" margin-top:0px; margin-bottom:0px; margin-left:0px; margin-right:0px; -qt-block-indent:0; text-indent:0px;"><span style=" font-size:10pt;">1 kom</span></p></body></html>
  LockPosition = false
  MaxWidth = -1
  Rotation = 0
  Scale = 0.5
  ScaleType = 0
  ShowFrame = false
  X = -76.7192
  Y = -6.01719
FEATURE [TechDraw::DrawRichAnno] RichTextAnnotation004
  AnnoParent = -> ProjItem002
  AnnoText = <!DOCTYPE HTML PUBLIC "-//W3C//DTD HTML 4.0//EN" "http://www.w3.org/TR/REC-html40/strict.dtd">\n<html><head><meta name="qrichtext" content="1" /><style type="text/css">\np, li { white-space: pre-wrap; }\n</style></head><body style=" font-family:'Ubuntu'; font-size:11pt; font-weight:400; font-style:normal;">\n<p style=" margin-top:0px; margin-bottom:0px; margin-left:0px; margin-right:0px; -qt-block-indent:0; text-indent:0px;"><span style=" font-size:10pt;">1 kom</span></p></body></html>
  LockPosition = false
  MaxWidth = -1
  Rotation = 0
  Scale = 0.5
  ScaleType = 0
  ShowFrame = false
  X = -78.8252
  Y = -6.01719
FEATURE [TechDraw::DrawPage] Page
  KeepUpdated = true
  NextBalloonIndex = 1
  ProjectionType = 0
  Scale = 0.5
  Template = -> Template
  Views = -> [ProjGroup,Dimension,Dimension001,Dimension002,Dimension003,Dimension004,Dimension005,Dimension006,ProjGroup001,ProjGroup004,Dimension009,Dimension010,RichTextAnnotation,RichTextAnnotation001,RichTextAnnotation002,RichTextAnnotation003,RichTextAnnotation004]
---- part streha.FCStd = doc fcstd_2c72739222b1 ----
FCSTD DOCUMENT  (FreeCAD 0.19R)
Label: streha
License: All rights reserved
LicenseURL: http://en.wikipedia.org/wiki/All_rights_reserved
objects: Sketcher::SketchObject×8, PartDesign::CoordinateSystem×7, TechDraw::DrawProjGroupItem×6, TechDraw::DrawViewDimension×6, App::Link×5, PartDesign::Pocket×4, App::Part×4, App::DocumentObjectGroup×3, PartDesign::Pad×3, PartDesign::Body×3, TechDraw::DrawProjGroup×3, TechDraw::DrawRichAnno×3, App::FeaturePython×1, TechDraw::DrawSVGTemplate×1, TechDraw::DrawViewPart×1, TechDraw::DrawPage×1
note: 32 computed .brp shape members not serialized (recipe doc carries the construction recipe); baked Part::Feature solids carry a one-line shape summary decoded from their .brp

FEATURE [PartDesign::CoordinateSystem] LCS_Origin
  AttacherType = Attacher::AttachEngine3D
  MapMode = 2
  Support = -> [X_Axis]
FEATURE [App::FeaturePython] Variables  # WARN: FeaturePython — macro-defined, semantics opaque (R4)
  Type = App::PropertyContainer
  bottom_thickness = 18
  inner_depth = 450
  inner_width = 375
  wall_thickness = 27
FEATURE [App::DocumentObjectGroup] Constraints
FEATURE [App::DocumentObjectGroup] Configurations
FEATURE [PartDesign::CoordinateSystem] LCS_0004
  AttacherType = Attacher::AttachEngine3D
  MapMode = 2
  Support = -> [X_Axis005]
FEATURE [PartDesign::CoordinateSystem] LCS_0005
  AttacherType = Attacher::AttachEngine3D
  MapMode = 2
  Support = -> [X_Axis006]
FEATURE [Sketcher::SketchObject] Sketch003  label="Sketch004"
  FullyConstrained = true
  MapMode = 5
  Placement = pos=(0,0,0) rot=(1,0,0;1.5708rad)
  Support = -> [XZ_Plane006]
  expr: Constraints[12] = Variables.inner_width / 2 + Variables.wall_thickness
  sketch-geometry (6):
    g0: LineSegment StartX=214.5 StartY=0 StartZ=0 EndX=218.5 EndY=0 EndZ=0
    g1: LineSegment StartX=218.5 StartY=0 StartZ=0 EndX=218.5 EndY=-8 EndZ=0
    g2: LineSegment StartX=218.5 StartY=-8 StartZ=0 EndX=226.5 EndY=-8 EndZ=0
    g3: LineSegment StartX=226.5 StartY=-8 StartZ=0 EndX=226.5 EndY=25.6324 EndZ=0
    g4: LineSegment StartX=214.5 StartY=30 StartZ=0 EndX=214.5 EndY=0 EndZ=0
    g5: LineSegment StartX=214.5 StartY=30 StartZ=0 EndX=226.5 EndY=25.6324 EndZ=0
  constraints (18):
    c: Horizontal(g0)
    c: Coincident(g0,g1)
    c: Vertical(g1)
    c: Coincident(g1,g2)
    c: Horizontal(g2)
    c: Coincident(g2,g3)
    c: Vertical(g3)
    c: Coincident(g4,g0)
    c: Vertical(g4)
    c: DistanceX(g0,g0) = 4  'c'
    c: DistanceY(g1,g1) = 8  'd'
    c: Horizontal(g0,g-1)
    c: DistanceX(g-1,g0) = 214.5
    c: DistanceX(g0,g2) = 12  'a'
    c: DistanceY(g4,g4) = 30  'b'
    c: Coincident(g5,g4)
    c: Coincident(g5,g3)
    c: Angle(g5) = -0.349066  'e'
FEATURE [PartDesign::Pad] Pad002
  Direction = (1,1,1)
  Length = 700
  Length2 = 100
  Midplane = true
  Placement = pos=(0,0,0) rot=(1,0,0;1.5708rad)
  Profile = -> Sketch003
  Type = 0
FEATURE [Sketcher::SketchObject] Sketch004  label="Sketch005"
  ExternalGeometry = -> [Pad002]
  FullyConstrained = true
  MapMode = 5
  Support = -> [XY_Plane006]
  expr: Constraints[14] = Variables.inner_depth + 2 * Variables.wall_thickness
  sketch-geometry (8):
    g0: LineSegment StartX=226.5 StartY=-350 StartZ=0 EndX=226.5 EndY=-264 EndZ=0
    g1: LineSegment StartX=226.5 StartY=-264 StartZ=0 EndX=214.5 EndY=-252 EndZ=0
    g2: LineSegment StartX=214.5 StartY=-252 StartZ=0 EndX=214.5 EndY=-350 EndZ=0
    g3: LineSegment StartX=226.5 StartY=350 StartZ=0 EndX=226.5 EndY=264 EndZ=0
    g4: LineSegment StartX=226.5 StartY=264 StartZ=0 EndX=214.5 EndY=252 EndZ=0
    g5: LineSegment StartX=214.5 StartY=252 StartZ=0 EndX=214.5 EndY=350 EndZ=0
    g6: LineSegment StartX=214.5 StartY=-350 StartZ=0 EndX=226.5 EndY=-350 EndZ=0
    g7: LineSegment StartX=214.5 StartY=350 StartZ=0 EndX=226.5 EndY=350 EndZ=0
  constraints (20):
    c: Coincident(g0,g-4)
    c: Coincident(g1,g0)
    c: Coincident(g2,g1)
    c: Coincident(g2,g-4)
    c: Vertical(g2)
    c: Vertical(g0)
    c: Coincident(g-3,g3)
    c: Vertical(g3)
    c: Coincident(g3,g4)
    c: Coincident(g4,g5)
    c: Coincident(g5,g-3)
    c: Vertical(g5)
    c: Equal(g4,g1)
    c: Equal(g5,g2)
    c: DistanceY(g1,g4) = 504
    c: Coincident(g6,g2)
    c: Coincident(g6,g0)
    c: Coincident(g7,g5)
    c: Coincident(g7,g3)
    c: Perpendicular(g4,g1)
FEATURE [PartDesign::Pocket] Pocket001
  BaseFeature = -> Pad002
  Length = 41
  Length2 = 100
  Midplane = true
  Placement = pos=(0,0,0) rot=(1,0,0;1.5708rad)
  Profile = -> Sketch004
  Type = 1
FEATURE [PartDesign::CoordinateSystem] LCS_0006
  AttacherType = Attacher::AttachEngine3D
  MapMode = 2
  Support = -> [X_Axis007]
FEATURE [PartDesign::CoordinateSystem] LCS_0007
  AttacherType = Attacher::AttachEngine3D
  MapMode = 2
  Support = -> [X_Axis008]
FEATURE [Sketcher::SketchObject] Sketch005  label="Sketch006"
  FullyConstrained = true
  MapMode = 5
  Placement = pos=(0,0,0) rot=(0.57735,0.57735,0.57735;2.0944rad)
  Support = -> [YZ_Plane008]
  expr: Constraints[17] = Variables.inner_depth / 2 + Variables.wall_thickness
  sketch-geometry (6):
    g0: LineSegment StartX=-252 StartY=0 StartZ=0 EndX=-252 EndY=30 EndZ=0
    g1: LineSegment StartX=-264 StartY=25.6324 StartZ=0 EndX=-264 EndY=-8 EndZ=0
    g2: LineSegment StartX=-264 StartY=-8 StartZ=0 EndX=-256 EndY=-8 EndZ=0
    g3: LineSegment StartX=-256 StartY=-8 StartZ=0 EndX=-256 EndY=0 EndZ=0
    g4: LineSegment StartX=-256 StartY=0 StartZ=0 EndX=-252 EndY=0 EndZ=0
    g5: LineSegment StartX=-264 StartY=25.6324 StartZ=0 EndX=-252 EndY=30 EndZ=0
  constraints (18):
    c: Vertical(g0)
    c: Vertical(g1)
    c: Coincident(g1,g2)
    c: Horizontal(g2)
    c: Coincident(g2,g3)
    c: Vertical(g3)
    c: Coincident(g3,g4)
    c: Coincident(g4,g0)
    c: Horizontal(g4)
    c: Horizontal(g0,g-1)
    c: DistanceX(g4,g4) = 4
    c: DistanceY(g3,g3) = 8
    c: DistanceX(g1,g0) = 12
    c: DistanceY(g0,g0) = 30
    c: Coincident(g5,g1)
    c: Coincident(g5,g0)
    c: Angle(g5) = 0.349066
    c: DistanceX(g0,g-1) = 252
FEATURE [PartDesign::Pad] Pad003
  Direction = (1,1,1)
  Length = 700
  Length2 = 100
  Midplane = true
  Placement = pos=(0,0,0) rot=(0.57735,0.57735,0.57735;2.0944rad)
  Profile = -> Sketch005
  Type = 0
FEATURE [Sketcher::SketchObject] Sketch006  label="Sketch007"
  ExternalGeometry = -> [Pad003]
  FullyConstrained = true
  MapMode = 5
  Support = -> [XY_Plane008]
  expr: Constraints[19] = Variables.inner_width + 2 * Variables.wall_thickness
  sketch-geometry (8):
    g0: LineSegment StartX=-350 StartY=-264 StartZ=0 EndX=-350 EndY=-252 EndZ=0
    g1: LineSegment StartX=-350 StartY=-252 StartZ=0 EndX=-214.5 EndY=-252 EndZ=0
    g2: LineSegment StartX=-214.5 StartY=-252 StartZ=0 EndX=-226.5 EndY=-264 EndZ=0
    g3: LineSegment StartX=-226.5 StartY=-264 StartZ=0 EndX=-350 EndY=-264 EndZ=0
    g4: LineSegment StartX=350 StartY=-264 StartZ=0 EndX=350 EndY=-252 EndZ=0
    g5: LineSegment StartX=350 StartY=-252 StartZ=0 EndX=214.5 EndY=-252 EndZ=0
    g6: LineSegment StartX=214.5 StartY=-252 StartZ=0 EndX=226.5 EndY=-264 EndZ=0
    g7: LineSegment StartX=226.5 StartY=-264 StartZ=0 EndX=350 EndY=-264 EndZ=0
  constraints (20):
    c: Coincident(g-3,g0)
    c: Coincident(g0,g-3)
    c: Coincident(g0,g1)
    c: Coincident(g1,g2)
    c: Coincident(g2,g3)
    c: Coincident(g3,g0)
    c: Coincident(g-4,g4)
    c: Coincident(g4,g-4)
    c: Coincident(g4,g5)
    c: Coincident(g5,g6)
    c: Coincident(g6,g7)
    c: Coincident(g7,g4)
    c: Perpendicular(g2,g6)
    c: Equal(g2,g6)
    c: Equal(g1,g5)
    c: Horizontal(g1)
    c: Horizontal(g3)
    c: Horizontal(g7)
    c: Horizontal(g5)
    c: DistanceX(g1,g5) = 429
FEATURE [PartDesign::Pocket] Pocket002
  BaseFeature = -> Pad003
  Length = 5
  Length2 = 100
  Midplane = true
  Placement = pos=(0,0,0) rot=(0.57735,0.57735,0.57735;2.0944rad)
  Profile = -> Sketch006
  Type = 1
FEATURE [App::Link] Slat003  label="slat_right"
  AssemblyType = Part::Link
  AttachedBy = #LCS_0004
  AttachedTo = Parent Assembly#LCS_Origin
  LinkedObject = -> Slat
  SolverId = Asm4EE
  expr: Placement = LCS_Origin.Placement * AttachmentOffset * LCS_0004.Placement ^ -1
FEATURE [App::Link] Slat2001  label="slat_front"
  AssemblyType = Part::Link
  AttachedBy = #LCS_0006
  AttachedTo = Parent Assembly#LCS_Origin
  LinkedObject = -> Slat2
  SolverId = Asm4EE
  expr: Placement = LCS_Origin.Placement * AttachmentOffset * LCS_0006.Placement ^ -1
FEATURE [App::Link] Slat2002  label="slat_left"
  AssemblyType = Part::Link
  AttachedBy = #LCS_0004
  AttachedTo = Parent Assembly#LCS_Origin
  AttachmentOffset = pos=(0,0,0) rot=(0,0,1;3.14159rad)
  LinkPlacement = pos=(0,0,0) rot=(0,0,1;3.14159rad)
  LinkedObject = -> Slat
  Placement = pos=(0,0,0) rot=(0,0,1;3.14159rad)
  SolverId = Asm4EE
  expr: Placement = LCS_Origin.Placement * AttachmentOffset * LCS_0004.Placement ^ -1
FEATURE [App::Link] Slat2003  label="slat_rear"
  AssemblyType = Part::Link
  AttachedBy = #LCS_0006
  AttachedTo = Parent Assembly#LCS_Origin
  AttachmentOffset = pos=(0,0,0) rot=(0,0,1;3.14159rad)
  LinkPlacement = pos=(0,0,0) rot=(0,0,1;3.14159rad)
  LinkedObject = -> Slat2
  Placement = pos=(0,0,0) rot=(0,0,1;3.14159rad)
  SolverId = Asm4EE
  expr: Placement = LCS_Origin.Placement * AttachmentOffset * LCS_0006.Placement ^ -1
FEATURE [TechDraw::DrawSVGTemplate] Template001
  EditableTexts = AVTOR=Brane Borštnik; AVTOR_2=Risal: Janez Paternoster; DATUM=6.5.2022; MATERIAL=Les, smreka; MERILO=1:5; NAZIV=Streha; NAZIV_2=Dadant-Blatt panj; STRAN=Stran 1/1; VIR=https://github.com/<owner>/Dadant-Blatt
  Height = 297
  Orientation = 0
  Width = 210
FEATURE [PartDesign::CoordinateSystem] LCS_0010
  AttacherType = Attacher::AttachEngine3D
  MapMode = 2
  Support = -> [X_Axis011]
FEATURE [PartDesign::CoordinateSystem] LCS_0011
  AttacherType = Attacher::AttachEngine3D
  MapMode = 2
  Support = -> [X_Axis012]
FEATURE [Sketcher::SketchObject] Sketch007  label="Sketch008"
  FullyConstrained = true
  MapMode = 5
  Support = -> [XY_Plane012]
  expr: Constraints[12] = Variables.inner_depth + Variables.wall_thickness * 2
  expr: Constraints[11] = Variables.inner_width + Variables.wall_thickness * 2
  sketch-geometry (5):
    g0: LineSegment StartX=214.5 StartY=252 StartZ=0 EndX=-214.5 EndY=252 EndZ=0
    g1: LineSegment StartX=-214.5 StartY=252 StartZ=0 EndX=-214.5 EndY=-252 EndZ=0
    g2: LineSegment StartX=-214.5 StartY=-252 StartZ=0 EndX=214.5 EndY=-252 EndZ=0
    g3: LineSegment StartX=214.5 StartY=-252 StartZ=0 EndX=214.5 EndY=252 EndZ=0
    g4: Circle CenterX=0 CenterY=0 CenterZ=0 NormalX=0 NormalY=0 NormalZ=1 AngleXU=0 Radius=330.929
  constraints (14):
    c: Coincident(g0,g1)
    c: Coincident(g1,g2)
    c: Coincident(g2,g3)
    c: Coincident(g3,g0)
    c: Equal(g0,g2)
    c: PointOnObject(g0,g4)
    c: PointOnObject(g1,g4)
    c: PointOnObject(g2,g4)
    c: PointOnObject(g3,g4)
    c: Coincident(g4,g-1)
    c: Horizontal(g2)
    c: DistanceX(g0,g0) = 429
    c: DistanceY(g3,g3) = 504
    c: Vertical(g1)
FEATURE [PartDesign::Pad] Pad004
  Direction = (1,1,1)
  Length = 18
  Length2 = 100
  Profile = -> Sketch007
  Type = 0
  expr: Length = Variables.bottom_thickness
FEATURE [App::Link] bottom001
  AssemblyType = Part::Link
  AttachedBy = #LCS_0010
  AttachedTo = Parent Assembly#LCS_Origin
  LinkedObject = -> bottom
  SolverId = Asm4EE
  expr: Placement = LCS_Origin.Placement * AttachmentOffset * LCS_0010.Placement ^ -1
FEATURE [App::Part] Assembly
  AssemblyType = Part::Link
  Group = -> [LCS_Origin,Constraints,Configurations,Slat003,Slat2001,Slat2002,Slat2003,bottom001]
  LabelDocUser = naklada
  LabelPartUser = Assembly
  Origin = -> Origin
  Type = Assembly
FEATURE [Sketcher::SketchObject] Sketch
  ExternalGeometry = -> [Pocket001]
  FullyConstrained = true
  MapMode = 5
  Placement = pos=(0,0,0) rot=(1,0,0;1.5708rad)
  Support = -> [XZ_Plane006]
  expr: Constraints[10] = Variables.bottom_thickness
  sketch-geometry (4):
    g0: LineSegment StartX=214.5 StartY=18 StartZ=0 EndX=226.5 EndY=18 EndZ=0
    g1: LineSegment StartX=226.5 StartY=18 StartZ=0 EndX=226.5 EndY=30 EndZ=0
    g2: LineSegment StartX=226.5 StartY=30 StartZ=0 EndX=214.5 EndY=30 EndZ=0
    g3: LineSegment StartX=214.5 StartY=30 StartZ=0 EndX=214.5 EndY=18 EndZ=0
  constraints (11):
    c: Coincident(g0,g1)
    c: Coincident(g1,g2)
    c: Coincident(g2,g3)
    c: Coincident(g3,g0)
    c: Horizontal(g0)
    c: Horizontal(g2)
    c: Vertical(g1)
    c: Vertical(g3)
    c: Coincident(g2,g-3)
    c: PointOnObject(g-3,g1)
    c: DistanceY(g-1,g0) = 18
FEATURE [PartDesign::Pocket] Pocket
  BaseFeature = -> Pocket001
  Length = 5
  Length2 = 100
  Midplane = true
  Placement = pos=(0,0,0) rot=(1,0,0;1.5708rad)
  Profile = -> Sketch
  Type = 1
FEATURE [PartDesign::Body] Body_3
  Group = -> [LCS_0005,Sketch003,Pad002,Sketch004,Pocket001,Sketch,Pocket]
  Origin = -> Origin006
  Tip = -> Pocket
FEATURE [App::Part] Slat  label="slat_side"
  Group = -> [LCS_0004,Body_3]
  Origin = -> Origin005
FEATURE [TechDraw::DrawProjGroupItem] ProjItem004  label="Front002"
  CoarseView = false
  Direction = (0,0,1)
  Focus = 100
  HardHidden = false
  IsoCount = 0
  IsoHidden = false
  IsoVisible = false
  LockPosition = true
  Perspective = false
  Rotation = 0
  RotationVector = (1,0,0)
  Scale = 0.2
  ScaleType = 2
  SeamHidden = false
  SeamVisible = true
  SmoothHidden = false
  SmoothVisible = true
  Source = -> [Slat]
  Type = 0
  X = 0
  XDirection = (1e-16,1,0)
  Y = 0
FEATURE [TechDraw::DrawProjGroupItem] ProjItem005  label="Left002"
  CoarseView = false
  Direction = (-1e-16,-1,1e-16)
  Focus = 100
  HardHidden = false
  IsoCount = 0
  IsoHidden = false
  IsoVisible = false
  LockPosition = false
  Perspective = false
  Rotation = 0
  RotationVector = (1,0,0)
  Scale = 0.2
  ScaleType = 2
  SeamHidden = false
  SeamVisible = true
  SmoothHidden = false
  SmoothVisible = true
  Source = -> [Slat]
  Type = 1
  X = 65.4
  XDirection = (0,1e-16,1)
  Y = 0
FEATURE [TechDraw::DrawProjGroup] ProjGroup002
  Anchor = -> ProjItem004
  AutoDistribute = true
  LockPosition = false
  ProjectionType = 0
  Rotation = 0
  Scale = 0.2
  ScaleType = 0
  Source = -> [Slat]
  Views = -> [ProjItem004,ProjItem005]
  X = 80.5609
  Y = 178.206
  spacingX = 10
  spacingY = 15
FEATURE [TechDraw::DrawViewDimension] Dimension023
  Arbitrary = false
  ArbitraryTolerances = false
  EqualTolerance = true
  FormatSpec = %.6g
  FormatSpecOverTolerance = %+.6g
  FormatSpecUnderTolerance = %+.6g
  Inverted = false
  LockPosition = false
  MeasureType = 1
  OverTolerance = 0
  References2D = -> [ProjItem004]
  Rotation = 0
  Scale = 0.2
  ScaleType = 0
  TheoreticalExact = false
  Type = 1
  UnderTolerance = 0
  X = -0.440729
  Y = 11.1164
FEATURE [TechDraw::DrawRichAnno] RichTextAnnotation
  AnnoParent = -> ProjItem004
  AnnoText = <!DOCTYPE HTML PUBLIC "-//W3C//DTD HTML 4.0//EN" "http://www.w3.org/TR/REC-html40/strict.dtd">\n<html><head><meta name="qrichtext" content="1" /><style type="text/css">\np, li { white-space: pre-wrap; }\n</style></head><body style=" font-family:'Ubuntu'; font-size:11pt; font-weight:400; font-style:normal;">\n<p style=" margin-top:0px; margin-bottom:0px; margin-left:0px; margin-right:0px; -qt-block-indent:0; text-indent:0px;"><span style=" font-size:10pt;">2 kom</span></p></body></html>
  LockPosition = false
  MaxWidth = -1
  Rotation = 0
  Scale = 0.2
  ScaleType = 0
  ShowFrame = false
  X = 56.6723
  Y = -5.45734
FEATURE [Sketcher::SketchObject] Sketch008  label="Sketch009"
  ExternalGeometry = -> [Pocket002]
  FullyConstrained = true
  MapMode = 5
  Placement = pos=(0,0,0) rot=(0.57735,0.57735,0.57735;2.0944rad)
  Support = -> [YZ_Plane008]
  expr: Constraints[10] = Variables.bottom_thickness
  sketch-geometry (4):
    g0: LineSegment StartX=-264 StartY=30 StartZ=0 EndX=-252 EndY=30 EndZ=0
    g1: LineSegment StartX=-252 StartY=30 StartZ=0 EndX=-252 EndY=18 EndZ=0
    g2: LineSegment StartX=-252 StartY=18 StartZ=0 EndX=-264 EndY=18 EndZ=0
    g3: LineSegment StartX=-264 StartY=18 StartZ=0 EndX=-264 EndY=30 EndZ=0
  constraints (11):
    c: Coincident(g0,g1)
    c: Coincident(g1,g2)
    c: Coincident(g2,g3)
    c: Coincident(g3,g0)
    c: Horizontal(g0)
    c: Horizontal(g2)
    c: Vertical(g1)
    c: Vertical(g3)
    c: Coincident(g0,g-3)
    c: PointOnObject(g-3,g3)
    c: DistanceY(g-1,g1) = 18
FEATURE [PartDesign::Pocket] Pocket003
  BaseFeature = -> Pocket002
  Length = 5
  Length2 = 100
  Midplane = true
  Placement = pos=(0,0,0) rot=(0.57735,0.57735,0.57735;2.0944rad)
  Profile = -> Sketch008
  Type = 1
FEATURE [PartDesign::Body] Body_4
  Group = -> [LCS_0007,Sketch005,Pad003,Sketch006,Pocket002,Sketch008,Pocket003]
  Origin = -> Origin008
  Tip = -> Pocket003
FEATURE [App::Part] Slat2  label="slat_front_rear"
  Group = -> [LCS_0006,Body_4]
  Origin = -> Origin007
FEATURE [TechDraw::DrawProjGroupItem] ProjItem006  label="Front003"
  CoarseView = false
  Direction = (0,0,1)
  Focus = 100
  HardHidden = false
  IsoCount = 0
  IsoHidden = false
  IsoVisible = false
  LockPosition = true
  Perspective = false
  Rotation = 0
  RotationVector = (1,0,0)
  Scale = 0.2
  ScaleType = 2
  SeamHidden = false
  SeamVisible = true
  SmoothHidden = false
  SmoothVisible = true
  Source = -> [Slat2]
  Type = 0
  X = 0
  XDirection = (1,0,0)
  Y = 0
FEATURE [TechDraw::DrawProjGroupItem] ProjItem007  label="Left003"
  CoarseView = false
  Direction = (-1,0,1e-16)
  Focus = 100
  HardHidden = false
  IsoCount = 0
  IsoHidden = false
  IsoVisible = false
  LockPosition = false
  Perspective = false
  Rotation = 0
  RotationVector = (1,0,0)
  Scale = 0.2
  ScaleType = 2
  SeamHidden = false
  SeamVisible = true
  SmoothHidden = false
  SmoothVisible = true
  Source = -> [Slat2]
  Type = 1
  X = 57.9
  XDirection = (1e-16,0,1)
  Y = 0
FEATURE [TechDraw::DrawProjGroup] ProjGroup003
  Anchor = -> ProjItem006
  AutoDistribute = true
  LockPosition = false
  ProjectionType = 0
  Rotation = 0
  Scale = 0.2
  ScaleType = 0
  Source = -> [Slat2]
  Views = -> [ProjItem006,ProjItem007]
  X = 76.6949
  Y = 154.558
  spacingX = 10
  spacingY = 15
FEATURE [TechDraw::DrawViewDimension] Dimension024
  Arbitrary = false
  ArbitraryTolerances = false
  EqualTolerance = true
  FormatSpec = %.6g
  FormatSpecOverTolerance = %+.6g
  FormatSpecUnderTolerance = %+.6g
  Inverted = false
  LockPosition = false
  MeasureType = 1
  OverTolerance = 0
  References2D = -> [ProjItem006]
  Rotation = 0
  Scale = 0.2
  ScaleType = 0
  TheoreticalExact = false
  Type = 1
  UnderTolerance = 0
  X = 0
  Y = 12.659
FEATURE [TechDraw::DrawRichAnno] RichTextAnnotation006
  AnnoParent = -> ProjItem006
  AnnoText = <!DOCTYPE HTML PUBLIC "-//W3C//DTD HTML 4.0//EN" "http://www.w3.org/TR/REC-html40/strict.dtd">\n<html><head><meta name="qrichtext" content="1" /><style type="text/css">\np, li { white-space: pre-wrap; }\n</style></head><body style=" font-family:'Ubuntu'; font-size:11pt; font-weight:400; font-style:normal;">\n<p style=" margin-top:0px; margin-bottom:0px; margin-left:0px; margin-right:0px; -qt-block-indent:0; text-indent:0px;"><span style=" font-size:10pt;">2 kom</span></p></body></html>
  LockPosition = false
  MaxWidth = -1
  Rotation = 0
  Scale = 0.2
  ScaleType = 0
  ShowFrame = false
  X = 49.7457
  Y = -4.61775
FEATURE [TechDraw::DrawViewPart] View
  CoarseView = false
  Direction = (0.577,-0.577,0.577)
  Focus = 100
  HardHidden = false
  IsoCount = 0
  IsoHidden = false
  IsoVisible = false
  LockPosition = false
  Perspective = false
  Rotation = 0
  Scale = 0.2
  ScaleType = 0
  SeamHidden = false
  SeamVisible = true
  SmoothHidden = false
  SmoothVisible = true
  Source = -> [Assembly]
  X = 103.749
  XDirection = (0.707,0.707,0)
  Y = 245.275
FEATURE [TechDraw::DrawRichAnno] RichTextAnnotation007
  AnnoParent = -> View
  AnnoText = <!DOCTYPE HTML PUBLIC "-//W3C//DTD HTML 4.0//EN" "http://www.w3.org/TR/REC-html40/strict.dtd">\n<html><head><meta name="qrichtext" content="1" /><style type="text/css">\np, li { white-space: pre-wrap; }\n</style></head><body style=" font-family:'Ubuntu'; font-size:11pt; font-weight:400; font-style:normal;">\n<p style=" margin-top:0px; margin-bottom:0px; margin-left:0px; margin-right:0px; -qt-block-indent:0; text-indent:0px;"><span style=" font-size:10pt;">Zgoraj prekrito s pločevino.</span></p></body></html>
  LockPosition = false
  MaxWidth = -1
  Rotation = 0
  Scale = 0.2
  ScaleType = 0
  ShowFrame = false
  X = 0
  Y = 0
FEATURE [Sketcher::SketchObject] Sketch009  label="Sketch010"
  FullyConstrained = true
  MapMode = 5
  Support = -> [XY_Plane012]
  expr: Constraints[9] = Variables.inner_depth
  expr: Constraints[8] = Variables.inner_width
  sketch-geometry (4):
    g0: LineSegment StartX=-187.5 StartY=-225 StartZ=0 EndX=187.5 EndY=-225 EndZ=0
    g1: LineSegment StartX=187.5 StartY=-225 StartZ=0 EndX=187.5 EndY=225 EndZ=0
    g2: LineSegment StartX=187.5 StartY=225 StartZ=0 EndX=-187.5 EndY=225 EndZ=0
    g3: LineSegment StartX=-187.5 StartY=225 StartZ=0 EndX=-187.5 EndY=-225 EndZ=0
  constraints (10):
    c: Coincident(g0,g1)
    c: Coincident(g1,g2)
    c: Coincident(g2,g3)
    c: Coincident(g3,g0)
    c: Horizontal(g2)
    c: Vertical(g3)
    c: Symmetric(g0,g0,g-2)
    c: Symmetric(g0,g1,g-1)
    c: DistanceX(g2,g2) = 375
    c: DistanceY(g3,g3) = 450
FEATURE [PartDesign::Body] Body_5
  Group = -> [LCS_0011,Sketch007,Pad004,Sketch009]
  Origin = -> Origin012
  Tip = -> Pad004
FEATURE [App::Part] bottom
  Group = -> [LCS_0010,Body_5]
  Origin = -> Origin011
FEATURE [App::DocumentObjectGroup] Parts
  Group = -> [Slat,Slat2,bottom]
FEATURE [TechDraw::DrawProjGroupItem] ProjItem  label="Front"
  CoarseView = false
  Direction = (0,0,-1)
  Focus = 100
  HardHidden = false
  IsoCount = 0
  IsoHidden = false
  IsoVisible = false
  LockPosition = true
  Perspective = false
  Rotation = 0
  RotationVector = (0,1,0)
  ScaleType = 2
  SeamHidden = false
  SeamVisible = true
  SmoothHidden = false
  SmoothVisible = true
  Source = -> [Body_5,Sketch009]
  Type = 0
  X = 0
  XDirection = (0,1,0)
  Y = 0
FEATURE [TechDraw::DrawProjGroupItem] ProjItem015  label="Left"
  CoarseView = false
  Direction = (0,-1,-1e-16)
  Focus = 100
  HardHidden = false
  IsoCount = 0
  IsoHidden = false
  IsoVisible = false
  LockPosition = false
  Perspective = false
  Rotation = 0
  RotationVector = (1,0,0)
  ScaleType = 2
  SeamHidden = false
  SeamVisible = true
  SmoothHidden = false
  SmoothVisible = true
  Source = -> [Body_5,Sketch009]
  Type = 1
  X = 67.2
  XDirection = (0,1e-16,-1)
  Y = 0
FEATURE [TechDraw::DrawProjGroup] ProjGroup
  Anchor = -> ProjItem
  AutoDistribute = true
  LockPosition = false
  ProjectionType = 0
  Rotation = 0
  Scale = 0.2
  ScaleType = 0
  Source = -> [Body_5,Sketch009]
  Views = -> [ProjItem,ProjItem015]
  X = 84.2366
  Y = 78.2168
  spacingX = 15
  spacingY = 15
FEATURE [TechDraw::DrawViewDimension] Dimension
  Arbitrary = false
  ArbitraryTolerances = false
  EqualTolerance = true
  FormatSpec = %.6g
  FormatSpecOverTolerance = %+.6g
  FormatSpecUnderTolerance = %+.6g
  Inverted = false
  LockPosition = false
  MeasureType = 1
  OverTolerance = 0
  References2D = -> [ProjItem]
  Rotation = 0
  Scale = 0.2
  ScaleType = 0
  TheoreticalExact = false
  Type = 1
  UnderTolerance = 0
  X = 1.31124
  Y = 64.4419
FEATURE [TechDraw::DrawViewDimension] Dimension025
  Arbitrary = false
  ArbitraryTolerances = false
  EqualTolerance = true
  FormatSpec = %.6g
  FormatSpecOverTolerance = %+.6g
  FormatSpecUnderTolerance = %+.6g
  Inverted = false
  LockPosition = false
  MeasureType = 1
  OverTolerance = 0
  References2D = -> [ProjItem]
  Rotation = 0
  Scale = 0.2
  ScaleType = 0
  TheoreticalExact = false
  Type = 2
  UnderTolerance = 0
  X = -60.328
  Y = 0.936603
FEATURE [TechDraw::DrawViewDimension] Dimension026
  Arbitrary = false
  ArbitraryTolerances = false
  EqualTolerance = true
  FormatSpec = %.6g
  FormatSpecOverTolerance = %+.6g
  FormatSpecUnderTolerance = %+.6g
  Inverted = false
  LockPosition = false
  MeasureType = 1
  OverTolerance = 0
  References2D = -> [ProjItem015]
  Rotation = 0
  Scale = 0.2
  ScaleType = 0
  TheoreticalExact = false
  Type = 1
  UnderTolerance = 0
  X = 9.92799
  Y = 63.3179
FEATURE [TechDraw::DrawViewDimension] Dimension027
  Arbitrary = false
  ArbitraryTolerances = false
  EqualTolerance = true
  FormatSpec = (debelina stene panja = %.6g)
  FormatSpecOverTolerance = %+.6g
  FormatSpecUnderTolerance = %+.6g
  Inverted = false
  LockPosition = false
  MeasureType = 1
  OverTolerance = 0
  References2D = -> [ProjItem]
  Rotation = 0
  Scale = 0.2
  ScaleType = 0
  TheoreticalExact = false
  Type = 1
  UnderTolerance = 0
  X = 9.29929
  Y = 54.0617
FEATURE [TechDraw::DrawPage] Page001  label="Page1"
  KeepUpdated = true
  NextBalloonIndex = 1
  ProjectionType = 0
  Scale = 0.2
  Template = -> Template001
  Views = -> [ProjGroup002,ProjGroup003,Dimension023,Dimension024,RichTextAnnotation,RichTextAnnotation006,View,RichTextAnnotation007,ProjGroup,Dimension,Dimension025,Dimension026,Dimension027]
